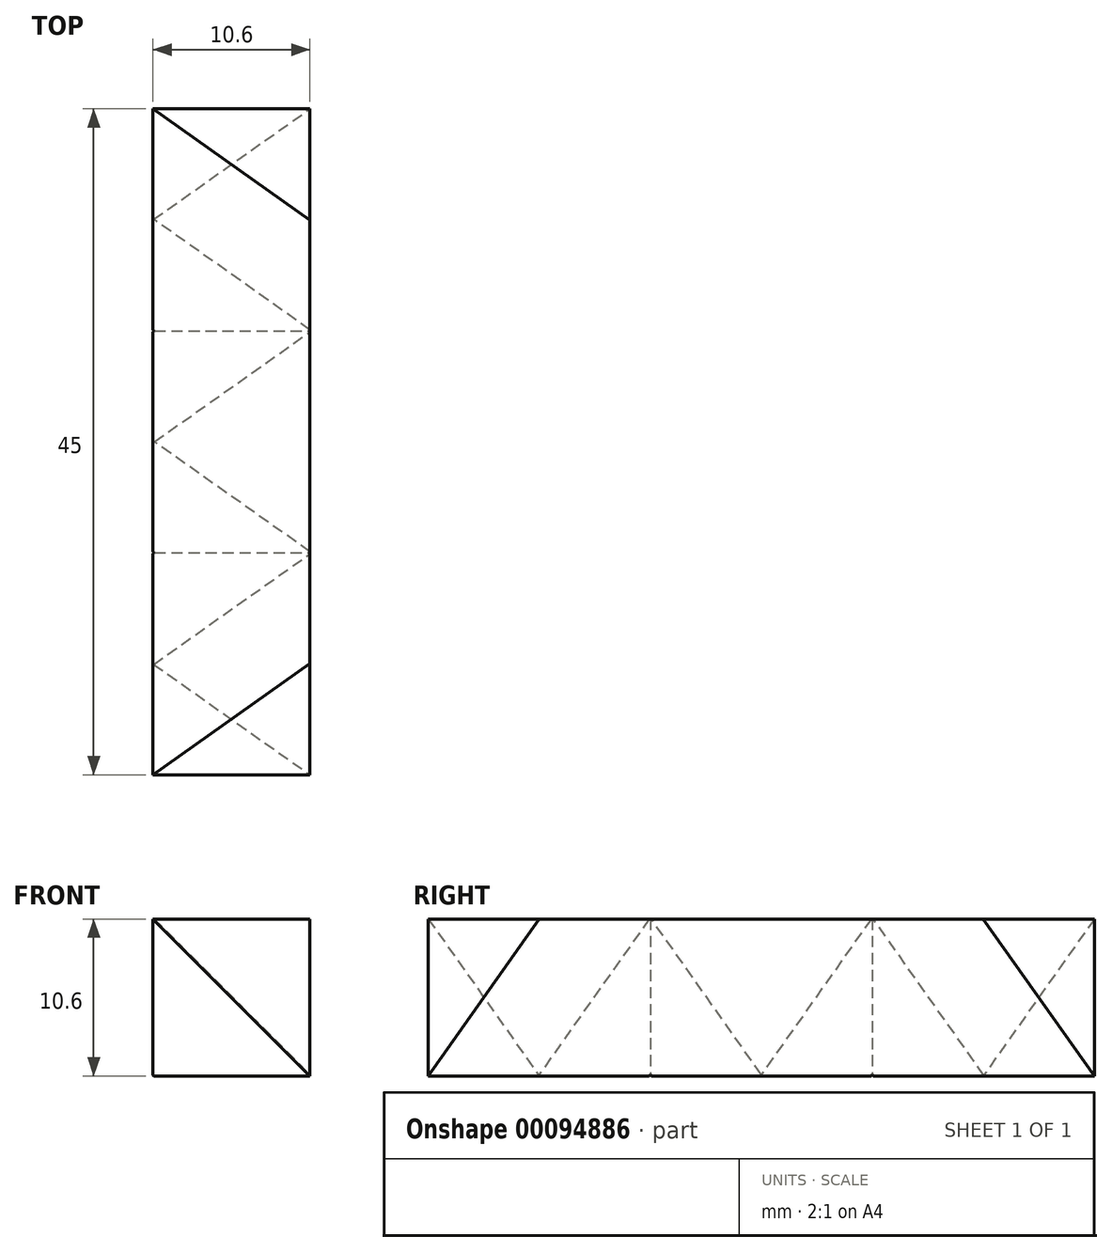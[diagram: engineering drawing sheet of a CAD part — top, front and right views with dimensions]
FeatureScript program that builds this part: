
annotation { "Feature Type Name" : "Feature", "Feature Type Description" : "" }
export const myFeature = defineFeature(function(context is Context, id is Id, definition is map)
    precondition{}
    {
        {
            var Q0;
            Q0=qCreatedBy(makeId("Front.planeOp"),FACE);
            var sketch = newSketch(context, id + "F0", { "sketchPlane" : qUnion([Q0])});
            skLineSegment(sketch, "E0.bottom", {"start": v(5.3, -5.3) * mm, "end": v(-5.3, -5.3) * mm});
            skLineSegment(sketch, "E0.top", {"start": v(5.3, 5.3) * mm, "end": v(-5.3, 5.3) * mm});
            skLineSegment(sketch, "E0.left", {"start": v(5.3, -5.3) * mm, "end": v(5.3, 5.3) * mm});
            skLineSegment(sketch, "E0.right", {"start": v(-5.3, -5.3) * mm, "end": v(-5.3, 5.3) * mm});
            skPoint(sketch, "E0.middle", {"position": v(0, 0) * mm});
            skSolve(sketch);
        }
        {
            var Q0;
            Q0 = qSketchRegion(id + "F0", true);
            extrude(context, id + "F1", {"entities" : qUnion([Q0]), "depth" : 45 * mm, "symmetric" : true});
        }
        {
            var Q0;
            Q0=makeQuery(id+"F1.opExtrude","CAP_VERTEX",VERTEX,{"disambiguationData":[OSD([sQuery(id+"F0.wireOp",EDGE,"E0.top"),sQuery(id+"F0.wireOp",EDGE,"E0.left")])],"isStart":false});
            var Q1;
            Q1=makeQuery(id+"F1.opExtrude","CAP_VERTEX",VERTEX,{"disambiguationData":[OSD([sQuery(id+"F0.wireOp",EDGE,"E0.top"),sQuery(id+"F0.wireOp",EDGE,"E0.left")])],"isStart":true});
            var Q2;
            Q2=makeQuery(id+"F1.opExtrude","CAP_VERTEX",VERTEX,{"disambiguationData":[OSD([sQuery(id+"F0.wireOp",EDGE,"E0.bottom"),sQuery(id+"F0.wireOp",EDGE,"E0.right")])],"isStart":true});
            cPlane(context, id + "F2", {"entities" : qUnion([Q0, Q1, Q2]), "cplaneType" : CPlaneType.THREE_POINT, "offset" : 0 * mm, "width" : 150 * mm, "height" : 150 * mm});
        }
        {
            var Q0;
            Q0=qCreatedBy(id+"F2.planeOp",FACE);
            var sketch = newSketch(context, id + "F3", { "sketchPlane" : qUnion([Q0])});
            skLineSegment(sketch, "E1", {"start": v(22.5, 0) * mm, "end": v(15, 7.5) * mm});
            skLineSegment(sketch, "E2", {"start": v(15, -7.5) * mm, "end": v(22.5, 0) * mm});
            skLineSegment(sketch, "E3", {"start": v(15, 7.5) * mm, "end": v(15, 9.5) * mm});
            skLineSegment(sketch, "E4", {"start": v(15, 9.5) * mm, "end": v(24.5, 9.5) * mm});
            skLineSegment(sketch, "E5", {"start": v(24.5, 9.5) * mm, "end": v(24.5, -9.5) * mm});
            skLineSegment(sketch, "E6", {"start": v(24.5, -9.5) * mm, "end": v(15, -9.5) * mm});
            skLineSegment(sketch, "E7", {"start": v(15, -9.5) * mm, "end": v(15, -7.5) * mm});
            skLineSegment(sketch, "E8", {"start": v(0, 16.28) * mm, "end": v(0, -17.75) * mm, "construction": true});
            skLineSegment(sketch, "E9.MirrorCS", {"start": v(-22.5, 0) * mm, "end": v(-15, 7.5) * mm});
            skLineSegment(sketch, "E10.MirrorCS", {"start": v(-15, 7.5) * mm, "end": v(-15, 9.5) * mm});
            skLineSegment(sketch, "E11.MirrorCS", {"start": v(-15, 9.5) * mm, "end": v(-24.5, 9.5) * mm});
            skLineSegment(sketch, "E12.MirrorCS", {"start": v(-24.5, 9.5) * mm, "end": v(-24.5, -9.5) * mm});
            skLineSegment(sketch, "E13.MirrorCS", {"start": v(-24.5, -9.5) * mm, "end": v(-15, -9.5) * mm});
            skLineSegment(sketch, "E14.MirrorCS", {"start": v(-15, -9.5) * mm, "end": v(-15, -7.5) * mm});
            skLineSegment(sketch, "E15.MirrorCS", {"start": v(-15, -7.5) * mm, "end": v(-22.5, 0) * mm});
            skSolve(sketch);
        }
        {
            var Q0;
            Q0=makeQuery(id+"F3.imprint","IMPRINT",FACE,{"disambiguationData":[TD([[makeQuery(id+"F3.imprint","IMPRINT",EDGE,{"derivedFrom":sQuery(id+"F3.wireOp",EDGE,"E9.MirrorCS")}),1.0]])]});
            var Q1;
            Q1=makeQuery(id+"F3.imprint","IMPRINT",FACE,{"disambiguationData":[TD([[makeQuery(id+"F3.imprint","IMPRINT",EDGE,{"derivedFrom":sQuery(id+"F3.wireOp",EDGE,"E1")}),-1.0]])]});
            extrude(context, id + "F4", {"entities" : qUnion([Q0, Q1]), "operationType" : NewBodyOperationType.REMOVE, "oppositeDirection" : true, "depth" : 30 * mm, "symmetric" : true});
        }
        {
            var Q0;
            Q0=qCreatedBy(id+"F2.planeOp",FACE);
            var sketch = newSketch(context, id + "F5", { "sketchPlane" : qUnion([Q0])});
            skLineSegment(sketch, "E16", {"start": v(0, -22.47) * mm, "end": v(0, 25.47) * mm, "construction": true});
            skLineSegment(sketch, "E17", {"start": v(0, -7.5) * mm, "end": v(-7.5, 0) * mm});
            skLineSegment(sketch, "E18", {"start": v(-7.5, 0) * mm, "end": v(-15, -7.5) * mm});
            skLineSegment(sketch, "E19", {"start": v(-15, -7.5) * mm, "end": v(-15, -9.5) * mm});
            skLineSegment(sketch, "E20", {"start": v(-7.5, -14.21) * mm, "end": v(-7.5, 5.7) * mm, "construction": true});
            skLineSegment(sketch, "E21", {"start": v(0, -7.5) * mm, "end": v(7.5, 0) * mm});
            skLineSegment(sketch, "E22", {"start": v(7.5, 0) * mm, "end": v(15, -7.5) * mm});
            skLineSegment(sketch, "E23", {"start": v(15, -7.5) * mm, "end": v(15, -9.5) * mm});
            skLineSegment(sketch, "E24", {"start": v(-15, -9.5) * mm, "end": v(15, -9.5) * mm});
            skLineSegment(sketch, "E25", {"start": v(7.5, -14.16) * mm, "end": v(7.5, 5.45) * mm, "construction": true});
            skSolve(sketch);
        }
        {
            var Q0;
            Q0=makeQuery(id+"F5.imprint","IMPRINT",FACE,{"disambiguationData":[TD([[makeQuery(id+"F5.imprint","IMPRINT",EDGE,{"derivedFrom":sQuery(id+"F5.wireOp",EDGE,"E17")}),1.0]])]});
            var Q1;
            Q1=makeQuery(id+"F5.imprint","IMPRINT",FACE,{"disambiguationData":[TD([[makeQuery(id+"F5.imprint","IMPRINT",EDGE,{"derivedFrom":sQuery(id+"F5.wireOp",EDGE,"fdc7fff6-2170-4d3c-9e52-04dbe153ffdc0.MirrorCS")}),-1.0]])]});
            extrude(context, id + "F6", {"entities" : qUnion([Q0, Q1]), "operationType" : NewBodyOperationType.REMOVE, "depth" : 30 * mm, "symmetric" : true});
        }
        {
            var Q0;
            Q0=qCreatedBy(id+"F2.planeOp",FACE);
            var sketch = newSketch(context, id + "F7", { "sketchPlane" : qUnion([Q0])});
            skLineSegment(sketch, "E26", {"start": v(-16.07, -8.5) * mm, "end": v(-7.5, 0.07) * mm});
            skLineSegment(sketch, "E27", {"start": v(-7.5, 0.07) * mm, "end": v(0, -7.43) * mm});
            skLineSegment(sketch, "E28", {"start": v(0, -7.43) * mm, "end": v(7.5, 0.07) * mm});
            skLineSegment(sketch, "E29", {"start": v(7.5, 0.07) * mm, "end": v(16.07, -8.5) * mm});
            skLineSegment(sketch, "E30", {"start": v(16.07, -8.5) * mm, "end": v(-16.07, -8.5) * mm});
            skSolve(sketch);
        }
        {
            var Q0;
            Q0=makeQuery(id+"F7.imprint","IMPRINT",FACE,{"disambiguationData":[TD([[makeQuery(id+"F7.imprint","IMPRINT",EDGE,{"derivedFrom":sQuery(id+"F7.wireOp",EDGE,"E26")}),-1.0]])]});
            extrude(context, id + "F8", {"entities" : qUnion([Q0]), "operationType" : NewBodyOperationType.REMOVE, "oppositeDirection" : true, "depth" : 30 * mm, "symmetric" : true});
        }
    });
